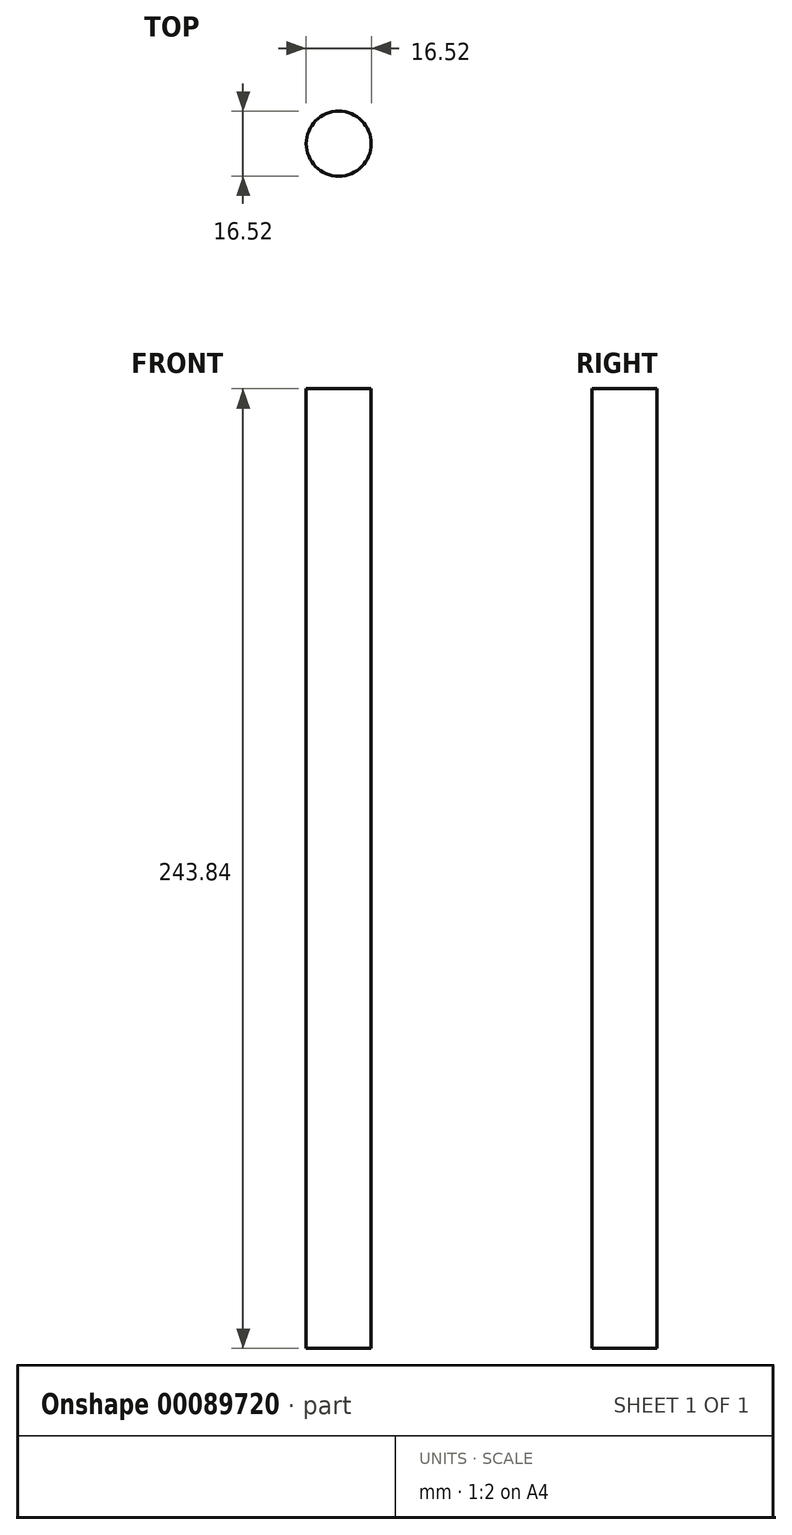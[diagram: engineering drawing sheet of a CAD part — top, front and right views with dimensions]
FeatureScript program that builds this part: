
annotation { "Feature Type Name" : "Feature", "Feature Type Description" : "" }
export const myFeature = defineFeature(function(context is Context, id is Id, definition is map)
    precondition{}
    {
        {
            var Q0;
            Q0=qCreatedBy(makeId("Top.planeOp"),FACE);
            var sketch = newSketch(context, id + "F0", { "sketchPlane" : qUnion([Q0])});
            skCircle(sketch, "E0", {"center": v(0, 0) * mm, "radius": 8.26 * mm});
            skSolve(sketch);
        }
        {
            var Q0;
            Q0=makeQuery(id+"F0.imprint","IMPRINT",FACE,{"disambiguationData":[TD([[makeQuery(id+"F0.imprint","IMPRINT",EDGE,{"derivedFrom":sQuery(id+"F0.wireOp",EDGE,"E0")}),1.0]])]});
            extrude(context, id + "F1", {"entities" : qUnion([Q0]), "depth" : 243.84 * mm});
        }
    });
